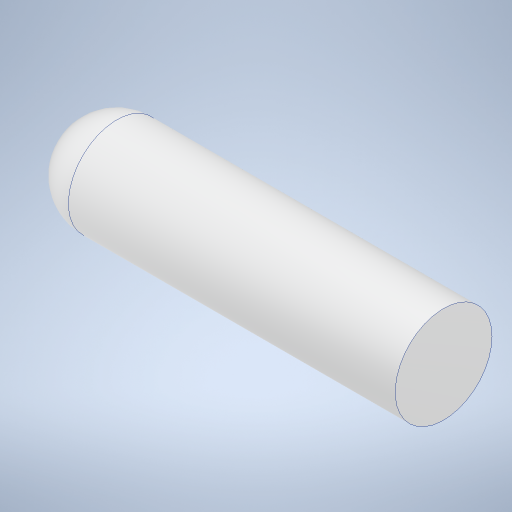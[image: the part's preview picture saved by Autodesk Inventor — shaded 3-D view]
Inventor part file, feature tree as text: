
AUTODESK INVENTOR PART (.ipt)
format: ipt  version: 2024 (Build 280153000, 153)  size: 235,520 bytes
history: native  units: mm
features: revolve x1, sketch x1
ambient origin geometry x8: Origin, YZ Plane, XZ Plane, XY Plane, X Axis, Y Axis, Z Axis, Center Point
bodies: Volumenkörper1 (feature_tree)
feature tree (2):
  revolve  "Umdrehung1"
  sketch  "Skizze1"  dims[d0=15.5mm d1=4.0mm d2=90.0deg]
